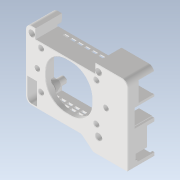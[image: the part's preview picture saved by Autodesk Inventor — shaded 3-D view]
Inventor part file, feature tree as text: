
AUTODESK INVENTOR PART (.ipt)
format: ipt  version: 2022.1 (Build 261234020, 234B)  size: 2,442,240 bytes
history: native  units: mm
features: projected_geometry x109, extrude x37, sketch x33, reference x32, chamfer x28, other x17, fillet x13, delete_face x13, move_body x6, direct_edit x5, hole x4
ambient origin geometry x8: Origin, YZ Plane, XZ Plane, XY Plane, X Axis, Y Axis, Z Axis, Center Point
bodies: Volumenkörper1 (feature_tree)
feature tree (297):
  extrude  "Extrusion1"  Depth=0.27499mm
  extrude  "Extrusion2"  Depth=0.6mm
  extrude  "Extrusion3"  Depth=0.6mm
  extrude  "Extrusion4"  Depth=0.6mm
  extrude  "Extrusion5"  Depth=0.4mm
  extrude  "Extrusion6"  Depth=1.6mm
  extrude  "Extrusion7"  Depth=3.0mm
  extrude  "Extrusion8"  Depth=3.0mm
  extrude  "Extrusion9"  Depth=12.0mm
  extrude  "Extrusion10"  Depth=0.6mm
  extrude  "Extrusion11"  Depth=0.2mm TaperAngle=0.0deg
  extrude  "Extrusion12"  Depth=2.8mm TaperAngle=0.0deg
  extrude  "Extrusion13"  Depth=2.6mm TaperAngle=0.0deg
  extrude  "Extrusion14"  Depth=7.2mm TaperAngle=0.0deg
  extrude  "Extrusion15"  Depth=1.0mm TaperAngle=0.0deg
  extrude  "Extrusion16"  Depth=3.2mm TaperAngle=0.0deg
  extrude  "Extrusion17"  Depth=0.6mm
  fillet  "Rundung1"  Radius=0.6mm
  extrude  "Extrusion18"  TaperAngle=0.0deg  [1 undecoded]
  fillet  "Rundung2"  Radius=0.8mm
  extrude  "Extrusion19"  Depth=1.2mm
  extrude  "Extrusion20"  Depth=10.0mm TaperAngle=0.0deg
  chamfer  "Fase1"  [1 undecoded]
  chamfer  "Fase2"  [1 undecoded]
  sketch  "Skizze21"  dims[d75=10.0mm d76=0.0mm d77=10.0mm d78=0.0mm]
  hole  "Bohrung1"  [1 undecoded]
  chamfer  "Fase3"  [1 undecoded]
  chamfer  "Fase4"  Distance=4.0mm
  hole  "Bohrung2"  [1 undecoded]
  chamfer  "Fase5"  Distance=4.0mm
  chamfer  "Fase6"  Distance=4.0mm
  direct_edit  "Direktbearbeitung1"
  extrude  "Extrusion21"  Depth=1.926931mm
  direct_edit  "Direktbearbeitung2"
  direct_edit  "Direktbearbeitung3"
  fillet  "Rundung3"  Radius=1.926931mm
  direct_edit  "Direktbearbeitung4"
  chamfer  "Fase7"  Distance=4.0mm
  delete_face  "Fläche löschen1"
  chamfer  "Fase8"  Distance=1.926931mm
  delete_face  "Fläche löschen2"
  chamfer  "Fase9"  Distance=1.926931mm
  chamfer  "Fase10"  Distance=1.926931mm
  chamfer  "Fase11"  Distance=3.0mm
  chamfer  "Fase12"  Distance=10.0mm
  extrude  "Extrusion22"  Depth=0.4mm TaperAngle=45.0deg
  chamfer  "Fase13"  Distance=0.4mm Angle=45.0deg
  delete_face  "Fläche löschen3"
  chamfer  "Fase14"  Distance=0.4mm Angle=45.0deg
  chamfer  "Fase15"  Distance=1.13mm Angle=45.0deg
  chamfer  "Fase16"  Distance=0.75mm Angle=45.0deg
  sketch  "Skizze24"  dims[d81=40.2mm]
  extrude  "Extrusion23"  Depth=0.4mm TaperAngle=45.0deg
  delete_face  "Fläche löschen4"
  delete_face  "Fläche löschen5"
  extrude  "Extrusion24"  Depth=1.2mm TaperAngle=0.0deg
  sketch  "Skizze26"  dims[d83=3.9mm]
  hole  "Bohrung3"  [1 undecoded]
  extrude  "Extrusion25"  Depth=0.8mm TaperAngle=0.0deg
  chamfer  "Fase17"  Distance=0.8mm
  fillet  "Rundung4"  Radius=2.0mm
  hole  "Bohrung4"  [1 undecoded]
  extrude  "Extrusion27"  Depth=0.4mm TaperAngle=0.0deg
  fillet  "Rundung5"  Radius=0.8mm
  direct_edit  "Direktbearbeitung5"
  delete_face  "Fläche löschen6"
  delete_face  "Fläche löschen7"
  delete_face  "Fläche löschen8"
  fillet  "Rundung6"  Radius=6.0mm
  extrude  "Extrusion28"  Depth=6.0mm TaperAngle=45.0deg
  extrude  "Extrusion29"  Depth=7.0mm TaperAngle=45.0deg
  chamfer  "Fase18"  Distance=4.0mm Angle=45.0deg
  delete_face  "Fläche löschen9"
  chamfer  "Fase19"  Distance=4.0mm Angle=45.0deg
  fillet  "Rundung7"  Radius=1.6mm
  chamfer  "Fase20"  Distance=4.0mm Angle=45.0deg
  chamfer  "Fase21"  Distance=4.0mm Angle=45.0deg
  fillet  "Rundung8"  Radius=4.0mm
  chamfer  "Fase22"  Distance=2.0mm Angle=45.0deg
  chamfer  "Fase23"  Distance=6.4mm
  fillet  "Rundung9"  Radius=10.4mm
  chamfer  "Fase24"  Distance=0.6mm
  chamfer  "Fase25"  Distance=18.0mm
  extrude  "Extrusion30"  TaperAngle=0.0deg  [1 undecoded]
  delete_face  "Fläche löschen10"
  delete_face  "Fläche löschen11"
  delete_face  "Fläche löschen12"
  chamfer  "Fase26"  Distance=33.634654mm
  fillet  "Rundung10"  Radius=33.634654mm
  extrude  "Extrusion31"  Depth=10.0mm TaperAngle=0.0deg
  chamfer  "Fase27"  Distance=6.7mm
  fillet  "Rundung11"  Radius=8.667706mm
  chamfer  "Fase28"  Distance=4.333853mm
  sketch  "Skizze34"  dims[d91=1.2mm]
  extrude  "Extrusion32"  Depth=6.7mm
  extrude  "Extrusion33"  TaperAngle=0.0deg  [1 undecoded]
  extrude  "Extrusion34"  Depth=33.0036mm
  fillet  "Rundung12"  Radius=16.5018mm
  delete_face  "Fläche löschen13"
  fillet  "Rundung13"  Radius=48.0mm
  sketch  "Skizze1"  dims[d0=9.2mm d1=0.27499mm]
  reference  "Referenz2"
  reference  "Referenz3"
  reference  "Referenz4"
  reference  "Referenz5"
  reference  "Referenz6"
  reference  "Referenz7"
  reference  "Referenz8"
  reference  "Referenz9"
  reference  "Referenz10"
  reference  "Referenz11"
  sketch  "Skizze2"  dims[d2=0.27499mm d3=0.6mm]
  projected_geometry  "Projizierte Kontur1"
  projected_geometry  "Projizierte Kontur2"
  projected_geometry  "Projizierte Kontur3"
  projected_geometry  "Projizierte Kontur4"
  reference  "Referenz12"
  reference  "Referenz13"
  reference  "Referenz14"
  reference  "Referenz15"
  reference  "Referenz16"
  sketch  "Skizze3"  dims[d4=0.6mm d5=0.6mm]
  reference  "Referenz17"
  reference  "Referenz18"
  reference  "Referenz19"
  reference  "Referenz20"
  projected_geometry  "Projizierte Kontur5"
  projected_geometry  "Projizierte Kontur6"
  projected_geometry  "Projizierte Kontur7"
  projected_geometry  "Projizierte Kontur8"
  projected_geometry  "Projizierte Kontur9"
  sketch  "Skizze4"  dims[d6=0.6mm d7=0.6mm]
  projected_geometry  "Projizierte Kontur10"
  projected_geometry  "Projizierte Kontur11"
  projected_geometry  "Projizierte Kontur12"
  projected_geometry  "Projizierte Kontur13"
  projected_geometry  "Projizierte Kontur14"
  projected_geometry  "Projizierte Kontur15"
  projected_geometry  "Projizierte Kontur16"
  projected_geometry  "Projizierte Kontur17"
  projected_geometry  "Projizierte Kontur18"
  projected_geometry  "Projizierte Kontur19"
  projected_geometry  "Projizierte Kontur20"
  projected_geometry  "Projizierte Kontur21"
  sketch  "Skizze5"  dims[d8=1.6mm d13=0.4mm]
  projected_geometry  "Projizierte Kontur22"
  projected_geometry  "Projizierte Kontur23"
  projected_geometry  "Projizierte Kontur24"
  projected_geometry  "Projizierte Kontur25"
  projected_geometry  "Projizierte Kontur26"
  projected_geometry  "Projizierte Kontur27"
  projected_geometry  "Projizierte Kontur28"
  projected_geometry  "Projizierte Kontur29"
  projected_geometry  "Projizierte Kontur30"
  projected_geometry  "Projizierte Kontur31"
  reference  "Referenz21"
  projected_geometry  "Projizierte Kontur32"
  sketch  "Skizze6"  dims[d14=1.6mm d24=1.6mm]
  projected_geometry  "Projizierte Kontur33"
  projected_geometry  "Projizierte Kontur34"
  projected_geometry  "Projizierte Kontur35"
  projected_geometry  "Projizierte Kontur36"
  projected_geometry  "Projizierte Kontur37"
  projected_geometry  "Projizierte Kontur38"
  projected_geometry  "Projizierte Kontur39"
  projected_geometry  "Projizierte Kontur40"
  projected_geometry  "Projizierte Kontur41"
  projected_geometry  "Projizierte Kontur42"
  reference  "Referenz22"
  reference  "Referenz23"
  projected_geometry  "Projizierte Kontur43"
  sketch  "Skizze7"  dims[d25=0.0mm d26=3.0mm]
  projected_geometry  "Projizierte Kontur44"
  projected_geometry  "Projizierte Kontur45"
  projected_geometry  "Projizierte Kontur46"
  projected_geometry  "Projizierte Kontur47"
  projected_geometry  "Projizierte Kontur48"
  projected_geometry  "Projizierte Kontur49"
  projected_geometry  "Projizierte Kontur50"
  projected_geometry  "Projizierte Kontur51"
  projected_geometry  "Projizierte Kontur52"
  projected_geometry  "Projizierte Kontur53"
  sketch  "Skizze8"  dims[d28=1.6mm d29=3.0mm]
  projected_geometry  "Projizierte Kontur54"
  projected_geometry  "Projizierte Kontur55"
  projected_geometry  "Projizierte Kontur56"
  projected_geometry  "Projizierte Kontur57"
  projected_geometry  "Projizierte Kontur58"
  projected_geometry  "Projizierte Kontur59"
  projected_geometry  "Projizierte Kontur60"
  projected_geometry  "Projizierte Kontur61"
  projected_geometry  "Projizierte Kontur62"
  sketch  "Skizze9"  dims[d31=1.6mm d32=12.0mm]
  projected_geometry  "Projizierte Kontur63"
  projected_geometry  "Projizierte Kontur64"
  projected_geometry  "Projizierte Kontur65"
  projected_geometry  "Projizierte Kontur66"
  projected_geometry  "Projizierte Kontur67"
  projected_geometry  "Projizierte Kontur68"
  projected_geometry  "Projizierte Kontur69"
  projected_geometry  "Projizierte Kontur70"
  projected_geometry  "Projizierte Kontur71"
  reference  "Referenz24"
  sketch  "Skizze10"  dims[d34=0.4mm d35=0.6mm]
  projected_geometry  "Projizierte Kontur72"
  sketch  "Skizze11"  dims[d36=0.6mm d37=0.2mm d38=0.0mm]
  reference  "Referenz25"
  reference  "Referenz26"
  reference  "Referenz27"
  reference  "Referenz28"
  projected_geometry  "Projizierte Kontur73"
  projected_geometry  "Projizierte Kontur74"
  reference  "Referenz29"
  reference  "Referenz30"
  reference  "Referenz31"
  sketch  "Skizze12"  dims[d39=6.3mm d40=2.8mm d41=0.0mm]
  projected_geometry  "Projizierte Kontur75"
  sketch  "Skizze13"  dims[d42=0.8mm d43=0.0mm d44=2.6mm d45=0.0mm]
  projected_geometry  "Projizierte Kontur76"
  reference  "Referenz32"
  projected_geometry  "Projizierte Kontur77"
  sketch  "Skizze14"  dims[d46=8.0mm d47=7.2mm d48=0.0mm]
  projected_geometry  "Projizierte Kontur78"
  projected_geometry  "Projizierte Kontur79"
  sketch  "Skizze15"  dims[d49=2.4mm d50=0.0mm d51=1.0mm d52=0.0mm]
  projected_geometry  "Projizierte Kontur80"
  sketch  "Skizze16"  dims[d53=5.0mm d54=0.0mm d55=3.2mm d56=0.0mm]
  projected_geometry  "Projizierte Kontur81"
  sketch  "Skizze17"  dims[d57=1.0mm d58=0.0mm d59=0.6mm d60=0.6mm]
  projected_geometry  "Projizierte Kontur82"
  projected_geometry  "Projizierte Kontur83"
  projected_geometry  "Projizierte Kontur84"
  projected_geometry  "Projizierte Kontur85"
  projected_geometry  "Projizierte Kontur86"
  projected_geometry  "Projizierte Kontur87"
  sketch  "Skizze18"  dims[d61=0.6mm d62=0.0mm d63=0.0mm d64=0.8mm]
  projected_geometry  "Projizierte Kontur88"
  projected_geometry  "Projizierte Kontur89"
  projected_geometry  "Projizierte Kontur90"
  projected_geometry  "Projizierte Kontur91"
  sketch  "Skizze19"  dims[d65=1.2mm d66=1.2mm]
  projected_geometry  "Projizierte Kontur92"
  projected_geometry  "Projizierte Kontur93"
  sketch  "Skizze20"  dims[d67=10.0mm d68=0.0mm d69=10.0mm d70=0.0mm d71=0.0mm d72=0.0mm d73=0.0mm d74=0.0mm]
  projected_geometry  "Projizierte Kontur94"
  projected_geometry  "Projizierte Kontur95"
  projected_geometry  "Projizierte Kontur96"
  projected_geometry  "Projizierte Kontur97"
  projected_geometry  "Projizierte Kontur98"
  projected_geometry  "Projizierte Kontur99"
  projected_geometry  "Projizierte Kontur100"
  projected_geometry  "Projizierte Kontur101"
  sketch  "Skizze22"  dims[d79=2.0mm]
  projected_geometry  "Projizierte Kontur102"
  projected_geometry  "Projizierte Kontur103"
  sketch  "Skizze23"  dims[d80=40.2mm]
  projected_geometry  "Projizierte Kontur104"
  sketch  "Skizze25"  dims[d82=3.9mm]
  projected_geometry  "Projizierte Kontur105"
  sketch  "Skizze27"  dims[d84=1.6mm d85=0.0mm d86=0.0mm]
  sketch  "Skizze29"  dims[d87=2.0mm]
  sketch  "Skizze31"  dims[d88=2.0mm]
  projected_geometry  "Projizierte Kontur109"
  projected_geometry  "Projizierte Kontur110"
  reference  "Referenz33"
  sketch  "Skizze32"  dims[d89=2.0mm]
  sketch  "Skizze33"  dims[d90=2.0mm]
  projected_geometry  "Projizierte Kontur111"
  projected_geometry  "Projizierte Kontur112"
  sketch  "Skizze35"  dims[d92=4.0mm d93=4.0mm d94=4.0mm d95=4.0mm d96=4.0mm d97=1.926931mm d98=1.926931mm d99=4.0mm d100=1.926931mm d101=1.926931mm d102=1.926931mm d103=3.0mm d104=0.0mm d105=10.0mm d106=0.0mm d107=0.4mm d108=2.0mm d109=45.0deg d110=0.4mm d111=2.0mm d112=45.0deg d113=3.34mm d114=6.0mm d115=5.6mm d116=11.2mm d117=90.0deg d118=8.0mm d119=20.594885mm d120=0.4mm d121=2.0mm d122=45.0deg d123=1.13mm d124=2.0mm d125=45.0deg d126=2.68mm d127=6.0mm d128=4.6mm d129=9.0mm d130=90.0deg d131=8.0mm d132=20.594885mm d133=0.75mm d134=2.0mm d135=45.0deg d136=0.4mm d137=2.0mm d138=45.0deg d139=0.0mm d140=0.0mm d141=1.2mm d142=1.6mm d143=0.0mm d144=0.0mm d145=0.0mm d146=0.8mm d147=0.0mm d148=0.0mm d149=0.8mm d150=2.0mm d151=0.0mm d152=0.0mm d153=0.4mm d154=0.0mm d155=0.0mm d156=0.4mm d157=0.8mm d158=2.0mm d159=45.0deg d160=6.0mm d161=2.0mm d162=45.0deg d163=6.0mm d164=2.0mm d165=45.0deg d166=7.0mm d167=2.0mm d168=45.0deg d169=4.0mm d170=2.0mm d171=45.0deg d172=4.0mm d173=2.0mm d174=45.0deg d175=1.6mm d176=0.0mm d177=4.0mm d178=2.0mm d179=45.0deg d180=4.0mm d181=2.0mm d182=45.0deg d183=4.0mm d184=2.0mm d185=45.0deg d186=2.0mm d187=2.0mm d188=45.0deg d189=6.4mm d190=10.4mm d191=0.6mm d193=18.0mm d194=0.0mm d195=2.0mm d196=2.0mm d197=2.0mm d198=1.2mm d199=4.0mm d200=4.0mm d201=4.0mm d202=4.0mm d203=4.0mm d204=1.926931mm d205=1.926931mm d206=4.0mm d207=1.926931mm d208=1.926931mm d209=1.926931mm d210=0.0mm d211=33.634654mm d212=33.634654mm d214=10.0mm d215=0.0mm d216=6.7mm d217=8.667706mm d218=4.333853mm d219=6.7mm d220=0.0mm d221=33.0036mm d222=16.5018mm d223=48.0mm d224=24.0mm d225=3.34mm d226=6.0mm d227=4.7mm d228=5.0mm d229=90.0deg d230=8.0mm d231=20.594885mm d232=1.2mm d233=1.2mm d234=1.2mm d235=3.0mm d236=0.0mm d237=1.0mm d238=2.0mm d239=45.0deg d240=1.0mm d241=3.34mm d242=6.0mm d243=4.7mm d244=5.0mm d245=90.0deg d246=8.0mm d247=20.594885mm d250=10.0mm d251=0.0mm d252=2.0mm d253=0.0mm d254=0.0mm d255=-0.2mm d256=18.0mm d257=0.0mm d258=0.0mm d259=9.0mm d260=0.0mm d261=2.12mm d262=2.0mm d263=45.0deg d264=4.0mm d265=2.0mm d266=45.0deg d267=100.0mm d268=1.4mm d269=2.0mm d270=45.0deg d271=1.4mm d272=2.0mm d273=45.0deg d274=5.0mm d275=1.4mm d276=2.0mm d277=45.0deg d278=1.4mm d279=2.0mm d280=45.0deg d281=5.0mm d282=1.2mm d283=0.34mm d284=2.0mm d285=45.0deg d286=0.4mm d287=2.0mm d288=45.0deg d289=0.4mm d290=0.4mm d291=0.0mm d292=0.0mm d293=1.4mm d294=2.0mm d295=45.0deg d296=5.0mm d297=3.0mm d298=4.0mm d299=0.0mm d300=2.0mm d301=2.0mm d302=45.0deg d303=5.0mm d304=1.0mm d305=2.0mm d306=45.0deg d307=12.8mm d308=14.4mm d309=17.0mm d310=0.0mm d311=1.2mm d312=4.0mm d313=0.0mm d314=10.0mm d315=0.0mm d316=4.0mm d317=4.0mm d318=4.0mm d319=4.0mm d322=4.0mm d324=2.198032mm d325=2.198032mm d326=2.198032mm d327=2.198032mm d328=2.198032mm d329=2.198032mm d330=2.198032mm d331=2.198032mm d332=4.0mm d333=4.0mm d334=4.0mm d335=2.198032mm d336=10.0mm d337=0.0mm d338=4.0mm d339=0.8mm]
  other  "<userpath>\Desktop\CM4Case\000_CM4-IO-BASE.iam"
  other  "000_CM4-IO-BASE.iam"
  other  "Board_1"
  other  "RJ1_200"
  extrude  "Extruded_198"  Depth=24.0mm
  extrude  "Extruded_190"  Depth=1.2mm
  other  "USB_HOST-2_267"
  other  "723095044blf_266"
  other  "HDMI0_226"
  other  "Case_CM4_Waveshare:1"
  other  "CM4-step:1"
  other  "Shapes"
  other  "SOLDERMASK_TOP"
  other  "PI1_168"
  extrude  "Extruded_107"  Depth=1.2mm
  extrude  "Extruded_105"  Depth=3.0mm TaperAngle=0.0deg
  other  "Symbols"
  other  "U21"
  move_body  "Verschieben1"
  move_body  "Verschieben2"
  move_body  "Verschieben3"
  move_body  "Verschieben4"
  move_body  "Verschieben5"
  move_body  "Verschieben6"
  other  "<userpath>\Desktop\GitHub\Voron-2-Mods\Arducam_IMX477_CM4\CM4\CAD\CM4_Case.iam"
  other  "CM4_Case.iam"
  other  "FanCover:1"
note: 10 required parameter values undecoded (feature->parameter linkage not recoverable at this tier; creation-order binding heuristic only, values carry confidence <= 0.55)
